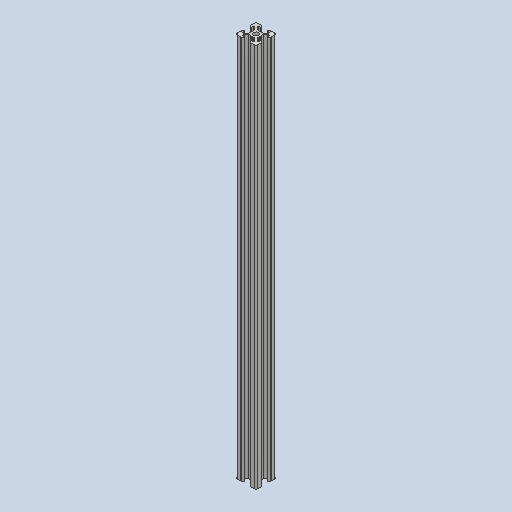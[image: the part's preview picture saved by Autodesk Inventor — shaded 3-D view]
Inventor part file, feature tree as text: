
AUTODESK INVENTOR PART (.ipt)
format: ipt  version: 2025.2 (Build 292293000, 293)  size: 406,528 bytes
history: native  units: mm
features: other x1, extrude x1, sketch x1
ambient origin geometry x8: Origin, YZ Plane, XZ Plane, XY Plane, X Axis, Y Axis, Z Axis, Center Point
bodies: Body1 (feature_tree)
feature tree (3):
  other  "Твердое тело1"
  extrude  "Выдавливание1"  Depth=0.25mm
  sketch  "Эскиз1"
